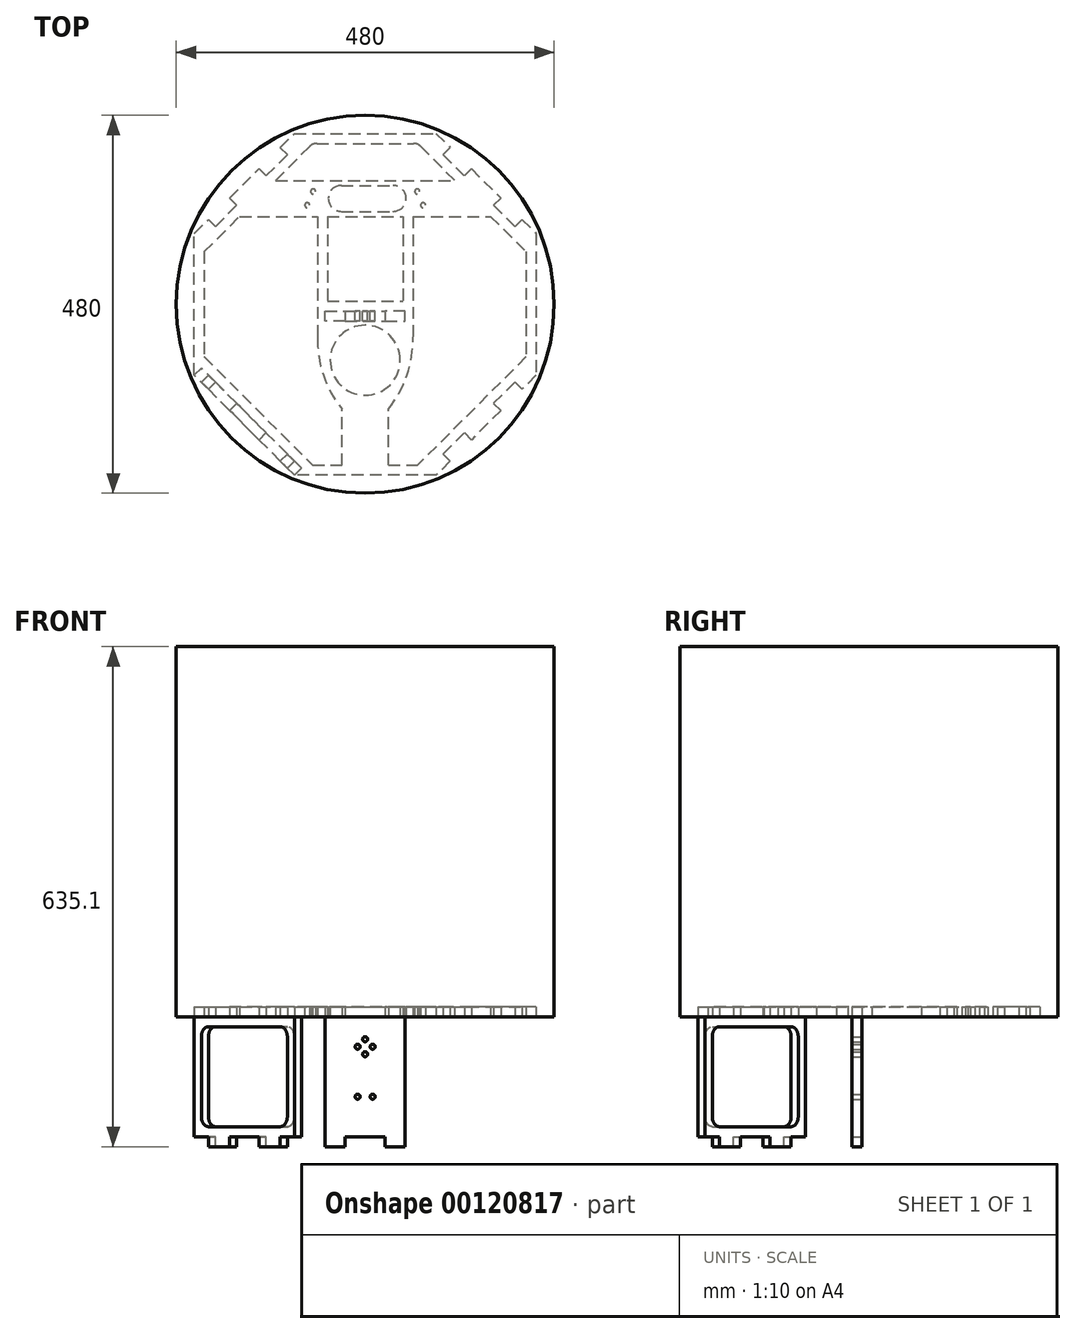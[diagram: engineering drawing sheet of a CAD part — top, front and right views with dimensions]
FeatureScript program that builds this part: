
annotation { "Feature Type Name" : "Feature", "Feature Type Description" : "" }
export const myFeature = defineFeature(function(context is Context, id is Id, definition is map)
    precondition{}
    {
        {
            var Q0;
            Q0=qCreatedBy(makeId("Top.planeOp"),FACE);
            var sketch = newSketch(context, id + "F0", { "sketchPlane" : qUnion([Q0])});
            skCircle(sketch, "E0", {"center": v(0, 0) * mm, "radius": 240 * mm});
            skSolve(sketch);
        }
        {
            var Q0;
            Q0=makeQuery(id+"F0.imprint","IMPRINT",FACE,{"disambiguationData":[TD([[makeQuery(id+"F0.imprint","IMPRINT",EDGE,{"derivedFrom":sQuery(id+"F0.wireOp",EDGE,"E0")}),1.0]])]});
            extrude(context, id + "F1", {"entities" : qUnion([Q0]), "depth" : 470 * mm});
        }
        {
            var Q0;
            Q0=qCreatedBy(makeId("Top.planeOp"),FACE);
            var sketch = newSketch(context, id + "F2", { "sketchPlane" : qUnion([Q0])});
            skCircle(sketch, "E1.cCircle", {"center": v(0, 0) * mm, "radius": 235 * mm, "construction": true});
            skLineSegment(sketch, "E1.0", {"start": v(89.93, 217.11) * mm, "end": v(107.9, 199.15) * mm});
            skLineSegment(sketch, "E1.1", {"start": v(217.11, 89.93) * mm, "end": v(217.11, -89.93) * mm});
            skLineSegment(sketch, "E1.2", {"start": v(217.11, -89.93) * mm, "end": v(199.15, -107.9) * mm});
            skLineSegment(sketch, "E1.3", {"start": v(89.93, -217.11) * mm, "end": v(-89.93, -217.11) * mm});
            skLineSegment(sketch, "E1.4", {"start": v(-89.93, -217.11) * mm, "end": v(-107.9, -199.15) * mm});
            skLineSegment(sketch, "E1.5", {"start": v(-217.11, -89.93) * mm, "end": v(-217.11, 89.93) * mm});
            skLineSegment(sketch, "E1.6", {"start": v(-217.11, 89.93) * mm, "end": v(-199.15, 107.9) * mm});
            skLineSegment(sketch, "E1.7", {"start": v(-89.93, 217.11) * mm, "end": v(89.93, 217.11) * mm});
            skLineSegment(sketch, "E2", {"start": v(-217.11, -89.93) * mm, "end": v(-199.15, -107.9) * mm});
            skLineSegment(sketch, "E3", {"start": v(-199.15, -107.9) * mm, "end": v(-190.17, -98.91) * mm});
            skLineSegment(sketch, "E4", {"start": v(-190.17, -98.91) * mm, "end": v(-163.23, -125.85) * mm});
            skLineSegment(sketch, "E5", {"start": v(-163.23, -125.85) * mm, "end": v(-172.21, -134.83) * mm});
            skLineSegment(sketch, "E6", {"start": v(-107.9, -199.15) * mm, "end": v(-98.91, -190.17) * mm});
            skLineSegment(sketch, "E7", {"start": v(-98.91, -190.17) * mm, "end": v(-125.85, -163.23) * mm});
            skLineSegment(sketch, "E8", {"start": v(-125.85, -163.23) * mm, "end": v(-134.83, -172.21) * mm});
            skLineSegment(sketch, "E9.trimOffspring", {"start": v(-199.15, -107.9) * mm, "end": v(-217.11, -89.93) * mm});
            skLineSegment(sketch, "E10.trimOffspring", {"start": v(-134.83, -172.21) * mm, "end": v(-172.21, -134.83) * mm});
            skLineSegment(sketch, "E11.MirrorCS", {"start": v(199.15, -107.9) * mm, "end": v(190.17, -98.91) * mm});
            skLineSegment(sketch, "E12.MirrorCS", {"start": v(190.17, -98.91) * mm, "end": v(163.23, -125.85) * mm});
            skLineSegment(sketch, "E13.MirrorCS", {"start": v(163.23, -125.85) * mm, "end": v(172.21, -134.83) * mm});
            skLineSegment(sketch, "E14.MirrorCS", {"start": v(125.85, -163.23) * mm, "end": v(134.83, -172.21) * mm});
            skLineSegment(sketch, "E15.MirrorCS", {"start": v(98.91, -190.17) * mm, "end": v(125.85, -163.23) * mm});
            skLineSegment(sketch, "E16.MirrorCS", {"start": v(107.9, -199.15) * mm, "end": v(98.91, -190.17) * mm});
            skLineSegment(sketch, "E17.MirrorCS", {"start": v(-199.15, 107.9) * mm, "end": v(-190.17, 98.91) * mm});
            skLineSegment(sketch, "E18.MirrorCS", {"start": v(-190.17, 98.91) * mm, "end": v(-163.23, 125.85) * mm});
            skLineSegment(sketch, "E19.MirrorCS", {"start": v(-163.23, 125.85) * mm, "end": v(-172.21, 134.83) * mm});
            skLineSegment(sketch, "E20.MirrorCS", {"start": v(-125.85, 163.23) * mm, "end": v(-134.83, 172.21) * mm});
            skLineSegment(sketch, "E21.MirrorCS", {"start": v(-98.91, 190.17) * mm, "end": v(-125.85, 163.23) * mm});
            skLineSegment(sketch, "E22.MirrorCS", {"start": v(-107.9, 199.15) * mm, "end": v(-98.91, 190.17) * mm});
            skLineSegment(sketch, "E23.MirrorCS", {"start": v(98.91, 190.17) * mm, "end": v(125.85, 163.23) * mm});
            skLineSegment(sketch, "E24.MirrorCS", {"start": v(107.9, 199.15) * mm, "end": v(98.91, 190.17) * mm});
            skLineSegment(sketch, "E25.MirrorCS", {"start": v(125.85, 163.23) * mm, "end": v(134.83, 172.21) * mm});
            skLineSegment(sketch, "E26.MirrorCS", {"start": v(163.23, 125.85) * mm, "end": v(172.21, 134.83) * mm});
            skLineSegment(sketch, "E27.MirrorCS", {"start": v(190.17, 98.91) * mm, "end": v(163.23, 125.85) * mm});
            skLineSegment(sketch, "E28.MirrorCS", {"start": v(199.15, 107.9) * mm, "end": v(190.17, 98.91) * mm});
            skLineSegment(sketch, "E29.trimOffspring", {"start": v(-107.9, 199.15) * mm, "end": v(-89.93, 217.11) * mm});
            skLineSegment(sketch, "E30.trimOffspring", {"start": v(-172.21, 134.83) * mm, "end": v(-134.83, 172.21) * mm});
            skLineSegment(sketch, "E31.trimOffspring", {"start": v(134.83, 172.21) * mm, "end": v(172.21, 134.83) * mm});
            skLineSegment(sketch, "E32.trimOffspring", {"start": v(199.15, 107.9) * mm, "end": v(217.11, 89.93) * mm});
            skLineSegment(sketch, "E33", {"start": v(-73.57, 125.8) * mm, "end": v(-66.13, 143.33) * mm, "construction": true});
            skLineSegment(sketch, "E34", {"start": v(-78.62, 138.28) * mm, "end": v(-61.08, 130.84) * mm, "construction": true});
            skPoint(sketch, "E35", {"position": v(-69.85, 134.56) * mm});
            skLineSegment(sketch, "E36.MirrorCS", {"start": v(73.57, 125.8) * mm, "end": v(66.13, 143.33) * mm, "construction": true});
            skLineSegment(sketch, "E37.MirrorCS", {"start": v(78.62, 138.28) * mm, "end": v(61.08, 130.84) * mm, "construction": true});
            skCircle(sketch, "E38", {"center": v(-73.57, 125.8) * mm, "radius": 3.18 * mm});
            skCircle(sketch, "E39.MirrorC", {"center": v(-66.13, 143.33) * mm, "radius": 3.18 * mm});
            skCircle(sketch, "E40.MirrorC", {"center": v(66.13, 143.33) * mm, "radius": 3.18 * mm});
            skCircle(sketch, "E41.MirrorC", {"center": v(73.57, 125.8) * mm, "radius": 3.18 * mm});
            skLineSegment(sketch, "E42", {"start": v(-204.41, 66.7) * mm, "end": v(-159.42, 111.7) * mm});
            skLineSegment(sketch, "E43", {"start": v(70.43, 200.7) * mm, "end": v(113.7, 157.42) * mm});
            skLineSegment(sketch, "E44", {"start": v(204.41, -66.7) * mm, "end": v(66.7, -204.41) * mm});
            skLineSegment(sketch, "E45", {"start": v(-204.41, -66.7) * mm, "end": v(-66.7, -204.41) * mm});
            skLineSegment(sketch, "E46.trimOffspring", {"start": v(172.21, -134.83) * mm, "end": v(134.83, -172.21) * mm});
            skLineSegment(sketch, "E47.trimOffspring", {"start": v(107.9, -199.15) * mm, "end": v(89.93, -217.11) * mm});
            skLineSegment(sketch, "E48", {"start": v(-25.4, -21.46) * mm, "end": v(-50.8, -21.46) * mm});
            skLineSegment(sketch, "E49", {"start": v(-50.8, -21.46) * mm, "end": v(-50.8, -8.76) * mm});
            skLineSegment(sketch, "E50", {"start": v(-50.8, -8.76) * mm, "end": v(-25.4, -8.76) * mm});
            skLineSegment(sketch, "E51", {"start": v(-25.4, -8.76) * mm, "end": v(-25.4, -21.46) * mm});
            skLineSegment(sketch, "E52.MirrorCS", {"start": v(25.4, -8.76) * mm, "end": v(25.4, -21.46) * mm});
            skLineSegment(sketch, "E53.MirrorCS", {"start": v(50.8, -8.76) * mm, "end": v(25.4, -8.76) * mm});
            skLineSegment(sketch, "E54.MirrorCS", {"start": v(50.8, -21.46) * mm, "end": v(50.8, -8.76) * mm});
            skLineSegment(sketch, "E55.MirrorCS", {"start": v(25.4, -21.46) * mm, "end": v(50.8, -21.46) * mm});
            skLineSegment(sketch, "E56", {"start": v(-159.42, 111.7) * mm, "end": v(159.42, 111.7) * mm});
            skLineSegment(sketch, "E57", {"start": v(-113.7, 157.42) * mm, "end": v(113.7, 157.42) * mm});
            skLineSegment(sketch, "E58", {"start": v(-30.34, 151.07) * mm, "end": v(35.58, 151.07) * mm});
            skLineSegment(sketch, "E59", {"start": v(-30.34, 118.05) * mm, "end": v(35.58, 118.05) * mm});
            skArc(sketch, "E60", {"start": v(35.58, 118.05) * mm, "mid": v(52.09, 134.56) * mm, "end": v(35.58, 151.07) * mm});
            skArc(sketch, "E61", {"start": v(-30.34, 151.07) * mm, "mid": v(-46.85, 134.56) * mm, "end": v(-30.34, 118.05) * mm});
            skLineSegment(sketch, "E62", {"start": v(-61.45, 204.41) * mm, "end": v(61.45, 204.41) * mm});
            skPoint(sketch, "E63.visualSharp", {"position": v(-66.7, 204.41) * mm});
            skArc(sketch, "E63.filletArc", {"start": v(-61.45, 204.41) * mm, "mid": v(-66.3, 203.44) * mm, "end": v(-70.43, 200.7) * mm});
            skPoint(sketch, "E64.visualSharp", {"position": v(66.7, 204.41) * mm});
            skArc(sketch, "E64.filletArc", {"start": v(70.43, 200.7) * mm, "mid": v(66.3, 203.44) * mm, "end": v(61.45, 204.41) * mm});
            skPoint(sketch, "E65", {"position": v(69.85, 134.56) * mm});
            skLineSegment(sketch, "E66", {"start": v(-204.41, 66.7) * mm, "end": v(-204.41, -66.7) * mm});
            skLineSegment(sketch, "E67", {"start": v(204.41, 66.7) * mm, "end": v(204.41, -66.7) * mm});
            skLineSegment(sketch, "E68", {"start": v(-66.7, -204.41) * mm, "end": v(66.7, -204.41) * mm});
            skLineSegment(sketch, "E69.trimOffspring", {"start": v(-113.7, 157.42) * mm, "end": v(-70.43, 200.7) * mm});
            skLineSegment(sketch, "E70.trimOffspring", {"start": v(159.42, 111.7) * mm, "end": v(204.41, 66.7) * mm});
            skLineSegment(sketch, "E71", {"start": v(-29.47, -204.41) * mm, "end": v(-29.47, -133.2) * mm});
            skCircle(sketch, "E72", {"center": v(0, -71) * mm, "radius": 44.45 * mm});
            skLineSegment(sketch, "E73", {"start": v(-60.67, 111.7) * mm, "end": v(-60.67, -41.6) * mm});
            skLineSegment(sketch, "E74", {"start": v(-47.97, 111.7) * mm, "end": v(-47.97, 3.94) * mm});
            skArc(sketch, "E75", {"start": v(-60.67, -41.6) * mm, "mid": v(-52.98, -90.1) * mm, "end": v(-29.47, -133.2) * mm});
            skLineSegment(sketch, "E76.MirrorCS", {"start": v(47.97, 111.7) * mm, "end": v(47.97, 3.94) * mm});
            skLineSegment(sketch, "E77.MirrorCS", {"start": v(60.67, 111.7) * mm, "end": v(60.67, -41.6) * mm});
            skArc(sketch, "E78.MirrorCS", {"start": v(60.67, -41.6) * mm, "mid": v(52.98, -90.1) * mm, "end": v(29.47, -133.2) * mm});
            skLineSegment(sketch, "E79.MirrorCS", {"start": v(29.47, -204.41) * mm, "end": v(29.47, -133.2) * mm});
            skLineSegment(sketch, "E80", {"start": v(-47.97, 3.94) * mm, "end": v(47.97, 3.94) * mm});
            skSolve(sketch);
        }
        {
            var Q0;
            Q0=makeQuery(id+"F2.imprint","IMPRINT",FACE,{"disambiguationData":[TD([[makeQuery(id+"F2.imprint","IMPRINT",EDGE,{"derivedFrom":sQuery(id+"F2.wireOp",EDGE,"E1.0")}),-1.0]])]});
            var Q1;
            Q1=makeQuery(id+"F2.imprint","IMPRINT",FACE,{"disambiguationData":[TD([[makeQuery(id+"F2.imprint","IMPRINT",EDGE,{"derivedFrom":sQuery(id+"F2.wireOp",EDGE,"zAsyleuf-xBmb-UvvF-GY4s-AbrPt3S4brjY")}),-1.0]])]});
            var Q2;
            Q2=makeQuery(id+"F2.imprint","IMPRINT",FACE,{"disambiguationData":[TD([[makeQuery(id+"F2.imprint","IMPRINT",EDGE,{"derivedFrom":sQuery(id+"F2.wireOp",EDGE,"E48")}),1.0]])]});
            extrude(context, id + "F3", {"entities" : qUnion([Q0, Q1, Q2]), "depth" : 12.7 * mm});
        }
        {
            var Q0;
            Q0=makeQuery(id+"F3.opExtrude","SWEPT_FACE",FACE,{"disambiguationData":[OSD([sQuery(id+"F2.wireOp",EDGE,"E4")])]});
            var sketch = newSketch(context, id + "F4", { "sketchPlane" : qUnion([Q0])});
            skLineSegment(sketch, "E81.0", {"start": v(-64.53, 0) * mm, "end": v(-89.93, 0) * mm});
            skLineSegment(sketch, "E82.0", {"start": v(-64.53, 12.7) * mm, "end": v(-64.53, 0) * mm});
            skLineSegment(sketch, "E83.0", {"start": v(-64.53, 12.7) * mm, "end": v(-26.43, 12.7) * mm});
            skLineSegment(sketch, "E84.0", {"start": v(-26.43, 12.7) * mm, "end": v(-26.43, 0) * mm});
            skLineSegment(sketch, "E85.0", {"start": v(26.43, 0) * mm, "end": v(-26.43, 0) * mm});
            skLineSegment(sketch, "E86.0", {"start": v(26.43, 12.7) * mm, "end": v(26.43, 0) * mm});
            skLineSegment(sketch, "E87.0", {"start": v(64.53, 12.7) * mm, "end": v(26.43, 12.7) * mm});
            skLineSegment(sketch, "E88.0", {"start": v(64.53, 12.7) * mm, "end": v(64.53, 0) * mm});
            skLineSegment(sketch, "E89.0", {"start": v(89.93, 0) * mm, "end": v(64.53, 0) * mm});
            skLineSegment(sketch, "E90", {"start": v(-89.93, 0) * mm, "end": v(-89.93, -152.4) * mm});
            skLineSegment(sketch, "E91", {"start": v(89.93, 0) * mm, "end": v(89.93, -152.4) * mm});
            skLineSegment(sketch, "E92", {"start": v(-89.93, -76.2) * mm, "end": v(89.93, -76.2) * mm, "construction": true});
            skLineSegment(sketch, "E93.MirrorCS", {"start": v(-64.53, -152.4) * mm, "end": v(-89.93, -152.4) * mm});
            skLineSegment(sketch, "E94.MirrorCS", {"start": v(-64.53, -165.1) * mm, "end": v(-64.53, -152.4) * mm});
            skLineSegment(sketch, "E95.MirrorCS", {"start": v(-64.53, -165.1) * mm, "end": v(-26.43, -165.1) * mm});
            skLineSegment(sketch, "E96.MirrorCS", {"start": v(-26.43, -165.1) * mm, "end": v(-26.43, -152.4) * mm});
            skLineSegment(sketch, "E97.MirrorCS", {"start": v(26.43, -152.4) * mm, "end": v(-26.43, -152.4) * mm});
            skLineSegment(sketch, "E98.MirrorCS", {"start": v(26.43, -165.1) * mm, "end": v(26.43, -152.4) * mm});
            skLineSegment(sketch, "E99.MirrorCS", {"start": v(64.53, -165.1) * mm, "end": v(26.43, -165.1) * mm});
            skLineSegment(sketch, "E100.MirrorCS", {"start": v(64.53, -165.1) * mm, "end": v(64.53, -152.4) * mm});
            skLineSegment(sketch, "E101.MirrorCS", {"start": v(89.93, -152.4) * mm, "end": v(64.53, -152.4) * mm});
            skLineSegment(sketch, "E102.bottom", {"start": v(64.53, -12.7) * mm, "end": v(-64.53, -12.7) * mm});
            skLineSegment(sketch, "E102.top", {"start": v(64.53, -139.7) * mm, "end": v(-64.53, -139.7) * mm});
            skLineSegment(sketch, "E102.left", {"start": v(77.23, -25.4) * mm, "end": v(77.23, -127) * mm});
            skLineSegment(sketch, "E102.right", {"start": v(-77.23, -25.4) * mm, "end": v(-77.23, -127) * mm});
            skPoint(sketch, "E102.middle", {"position": v(0, -76.2) * mm});
            skPoint(sketch, "E103.visualSharp", {"position": v(-77.23, -12.7) * mm});
            skArc(sketch, "E103.filletArc", {"start": v(-64.53, -12.7) * mm, "mid": v(-73.51, -16.42) * mm, "end": v(-77.23, -25.4) * mm});
            skPoint(sketch, "E104.visualSharp", {"position": v(77.23, -12.7) * mm});
            skArc(sketch, "E104.filletArc", {"start": v(77.23, -25.4) * mm, "mid": v(73.51, -16.42) * mm, "end": v(64.53, -12.7) * mm});
            skPoint(sketch, "E105.visualSharp", {"position": v(-77.23, -139.7) * mm});
            skArc(sketch, "E105.filletArc", {"start": v(-77.23, -127) * mm, "mid": v(-73.51, -135.98) * mm, "end": v(-64.53, -139.7) * mm});
            skPoint(sketch, "E106.visualSharp", {"position": v(77.23, -139.7) * mm});
            skArc(sketch, "E106.filletArc", {"start": v(64.53, -139.7) * mm, "mid": v(73.51, -135.98) * mm, "end": v(77.23, -127) * mm});
            skSolve(sketch);
        }
        {
            var Q0;
            Q0=makeQuery(id+"F4.imprint","IMPRINT",FACE,{"disambiguationData":[TD([[makeQuery(id+"F4.imprint","IMPRINT",EDGE,{"derivedFrom":sQuery(id+"F4.wireOp",EDGE,"hkWFCvl3-0GtP-muFp-XwWA-r1syVBp0ultu")}),1.0]])]});
            var Q1;
            Q1=makeQuery(id+"F4.imprint","IMPRINT",FACE,{"disambiguationData":[TD([[makeQuery(id+"F4.imprint","IMPRINT",EDGE,{"derivedFrom":sQuery(id+"F4.wireOp",EDGE,"0LUAg8wl-BAx9-YgKv-2hv8-wQYNoT19xgKx")}),-1.0]])]});
            var Q2;
            Q2=makeQuery(id+"F4.imprint","IMPRINT",FACE,{"disambiguationData":[TD([[makeQuery(id+"F4.imprint","IMPRINT",EDGE,{"derivedFrom":sQuery(id+"F4.wireOp",EDGE,"E81.0")}),1.0]])]});
            var Q3;
            Q3=makeQuery(id+"F4.imprint","IMPRINT",FACE,{"disambiguationData":[TD([[makeQuery(id+"F4.imprint","IMPRINT",EDGE,{"derivedFrom":sQuery(id+"F4.wireOp",EDGE,"E82.0")}),1.0]])]});
            extrude(context, id + "F5", {"entities" : qUnion([Q0, Q1, Q2, Q3]), "depth" : 12.7 * mm});
        }
        {
            var Q0;
            Q0=makeQuery(id+"F3.opExtrude","SWEPT_FACE",FACE,{"disambiguationData":[OSD([sQuery(id+"F2.wireOp",EDGE,"E53.MirrorCS")])]});
            var sketch = newSketch(context, id + "F6", { "sketchPlane" : qUnion([Q0])});
            skLineSegment(sketch, "E107.0.1", {"start": v(-25.4, 0) * mm, "end": v(-25.4, 12.7) * mm});
            skLineSegment(sketch, "E107.0.2", {"start": v(-25.4, 12.7) * mm, "end": v(-50.8, 12.7) * mm});
            skLineSegment(sketch, "E107.0.3", {"start": v(-50.8, 12.7) * mm, "end": v(-50.8, 0) * mm});
            skLineSegment(sketch, "E108", {"start": v(-25.4, 0) * mm, "end": v(25.4, 0) * mm});
            skLineSegment(sketch, "E109", {"start": v(25.4, 0) * mm, "end": v(25.4, 12.7) * mm});
            skLineSegment(sketch, "E110", {"start": v(25.4, 12.7) * mm, "end": v(50.8, 12.7) * mm});
            skLineSegment(sketch, "E111", {"start": v(50.8, 12.7) * mm, "end": v(50.8, 0) * mm});
            skLineSegment(sketch, "E112", {"start": v(50.8, 0) * mm, "end": v(50.8, -152.4) * mm});
            skLineSegment(sketch, "E113", {"start": v(-50.8, 0) * mm, "end": v(-50.8, -152.4) * mm});
            skLineSegment(sketch, "E114", {"start": v(-50.8, -76.2) * mm, "end": v(50.8, -76.2) * mm, "construction": true});
            skLineSegment(sketch, "E115.MirrorCS", {"start": v(-50.8, -165.1) * mm, "end": v(-50.8, -152.4) * mm});
            skLineSegment(sketch, "E116.MirrorCS", {"start": v(-25.4, -165.1) * mm, "end": v(-50.8, -165.1) * mm});
            skLineSegment(sketch, "E117.MirrorCS", {"start": v(-25.4, -152.4) * mm, "end": v(-25.4, -165.1) * mm});
            skLineSegment(sketch, "E118.MirrorCS", {"start": v(-25.4, -152.4) * mm, "end": v(25.4, -152.4) * mm});
            skLineSegment(sketch, "E119.MirrorCS", {"start": v(25.4, -152.4) * mm, "end": v(25.4, -165.1) * mm});
            skLineSegment(sketch, "E120.MirrorCS", {"start": v(25.4, -165.1) * mm, "end": v(50.8, -165.1) * mm});
            skLineSegment(sketch, "E121.MirrorCS", {"start": v(50.8, -165.1) * mm, "end": v(50.8, -152.4) * mm});
            skLineSegment(sketch, "E122", {"start": v(0, -47.63) * mm, "end": v(0, -28.57) * mm, "construction": true});
            skPoint(sketch, "E122.startSnap0", {"position": v(0, -76.2) * mm});
            skLineSegment(sketch, "E123", {"start": v(-9.53, -38.1) * mm, "end": v(9.53, -38.1) * mm, "construction": true});
            skPoint(sketch, "E124", {"position": v(0, -38.1) * mm});
            skCircle(sketch, "E125", {"center": v(-9.53, -38.1) * mm, "radius": 3.18 * mm});
            skCircle(sketch, "E126", {"center": v(0, -47.63) * mm, "radius": 3.18 * mm});
            skCircle(sketch, "E127.MirrorC", {"center": v(0, -28.57) * mm, "radius": 3.18 * mm});
            skCircle(sketch, "E128.MirrorC", {"center": v(9.53, -38.1) * mm, "radius": 3.18 * mm});
            skLineSegment(sketch, "E129", {"start": v(-9.52, -101.6) * mm, "end": v(9.52, -101.6) * mm, "construction": true});
            skCircle(sketch, "E130", {"center": v(-9.52, -101.6) * mm, "radius": 3.18 * mm});
            skCircle(sketch, "E131.MirrorC", {"center": v(9.52, -101.6) * mm, "radius": 3.18 * mm});
            skPoint(sketch, "E132", {"position": v(0, -101.6) * mm});
            skSolve(sketch);
        }
        {
            var Q0;
            Q0 = qSketchRegion(id + "F6", true);
            extrude(context, id + "F7", {"entities" : qUnion([Q0]), "depth" : 12.7 * mm});
        }
    });
